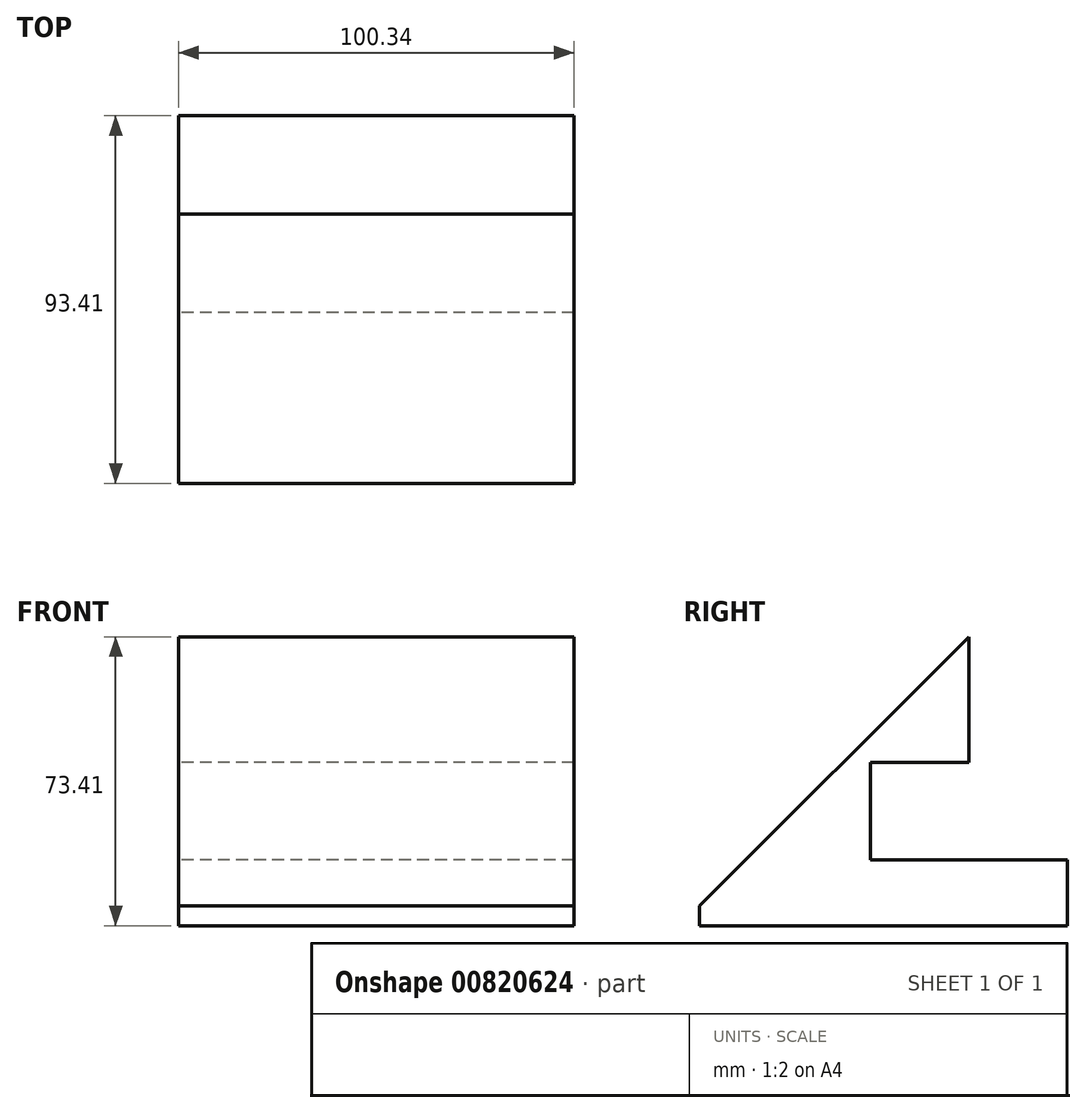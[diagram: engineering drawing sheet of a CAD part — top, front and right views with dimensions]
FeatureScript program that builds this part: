
annotation { "Feature Type Name" : "Feature", "Feature Type Description" : "" }
export const myFeature = defineFeature(function(context is Context, id is Id, definition is map)
    precondition{}
    {
        {
            var Q0;
            Q0=qCreatedBy(makeId("Top.planeOp"),FACE);
            var sketch = newSketch(context, id + "F0", { "sketchPlane" : qUnion([Q0])});
            skLineSegment(sketch, "E0.bottom", {"start": v(-52.53, 32.2) * mm, "end": v(47.81, 32.2) * mm});
            skLineSegment(sketch, "E0.top", {"start": v(-52.53, -36.2) * mm, "end": v(47.81, -36.2) * mm});
            skLineSegment(sketch, "E0.left", {"start": v(-52.53, 32.2) * mm, "end": v(-52.53, -36.2) * mm});
            skLineSegment(sketch, "E0.right", {"start": v(47.81, 32.2) * mm, "end": v(47.81, -36.2) * mm});
            skSolve(sketch);
        }
        {
            var Q0;
            Q0=makeQuery(id+"F0.imprint","IMPRINT",FACE,{"disambiguationData":[TD([[makeQuery(id+"F0.imprint","IMPRINT",EDGE,{"derivedFrom":sQuery(id+"F0.wireOp",EDGE,"E0.bottom")}),-1.0]])]});
            extrude(context, id + "F1", {"entities" : qUnion([Q0]), "depth" : 75 * mm, "offsetDistance" : 25 * mm});
        }
        {
            var Q0;
            Q0=makeQuery(id+"F1.opExtrude","CAP_EDGE",EDGE,{"disambiguationData":[OSD([sQuery(id+"F0.wireOp",EDGE,"E0.top")])],"isStart":false});
            chamfer(context, id + "F2", {"entities" : qUnion([Q0]), "width" : 70 * mm, "tangentPropagation" : true});
        }
        {
            var Q0;
            Q0=makeQuery(id+"F1.opExtrude","SWEPT_FACE",FACE,{"disambiguationData":[OSD([sQuery(id+"F0.wireOp",EDGE,"E0.bottom")])]});
            var sketch = newSketch(context, id + "F3", { "sketchPlane" : qUnion([Q0])});
            skLineSegment(sketch, "E1.bottom", {"start": v(-55.8, 41.46) * mm, "end": v(65.05, 41.46) * mm});
            skLineSegment(sketch, "E1.top", {"start": v(-55.8, 16.78) * mm, "end": v(65.05, 16.78) * mm});
            skLineSegment(sketch, "E1.left", {"start": v(-55.8, 41.46) * mm, "end": v(-55.8, 16.78) * mm});
            skLineSegment(sketch, "E1.right", {"start": v(65.05, 41.46) * mm, "end": v(65.05, 16.78) * mm});
            skSolve(sketch);
        }
        {
            var Q0;
            {var subQ0=sQuery(id+"F3.wireOp",EDGE,"E1.bottom");var subQ1=sQuery(id+"F0.wireOp",EDGE,"E0.bottom");var subQ2=makeQuery(id+"F1.opExtrude","SWEPT_EDGE",EDGE,{"disambiguationData":[OSD([subQ1,sQuery(id+"F0.wireOp",EDGE,"E0.right")])]});var subQ3=makeQuery(id+"F3.imprint","INTERSECT",VERTEX,{"derivedFrom":[subQ2,subQ0]});Q0=makeQuery(id+"F3.imprint","IMPRINT",FACE,{"disambiguationData":[TD([[makeQuery(id+"F3.imprint","IMPRINT",EDGE,{"disambiguationData":[TD([[subQ3,-1.0]])],"derivedFrom":subQ0}),-1.0]])]});}
            extrude(context, id + "F4", {"entities" : qUnion([Q0]), "operationType" : NewBodyOperationType.REMOVE, "oppositeDirection" : true, "depth" : 25 * mm, "offsetDistance" : 25 * mm});
        }
        {
            var Q0;
            {var subQ2=sQuery(id+"F0.wireOp",EDGE,"E0.bottom");Q0=makeQuery(id+"F4.boolean.opBoolean","SPLIT",FACE,{"disambiguationData":[TD([makeQuery(id+"F4.opExtrude","SWEPT_FACE",FACE,{"disambiguationData":[OSD([sQuery(id+"F3.wireOp",EDGE,"E1.top")])]})])],"derivedFrom":makeQuery(id+"F1.opExtrude","SWEPT_FACE",FACE,{"disambiguationData":[OSD([subQ2])]})});}
            extrude(context, id + "F5", {"entities" : qUnion([Q0]), "operationType" : NewBodyOperationType.ADD, "depth" : 25 * mm, "offsetDistance" : 25 * mm});
        }
    });
